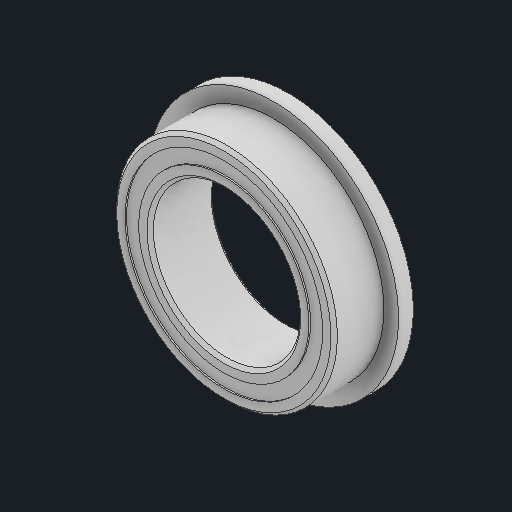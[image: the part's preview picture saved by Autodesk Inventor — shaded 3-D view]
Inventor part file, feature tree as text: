
AUTODESK INVENTOR PART (.ipt)
format: ipt  version: 2024 (Build 280153000, 153)  size: 592,896 bytes
history: native  units: in
note: dims shown in document units (in); Inventor stores cm internally (conversion verified against a paired STEP export)
features: other x11, revolve x5
ambient origin geometry x8: Origin, YZ Plane, XZ Plane, XY Plane, X Axis, Y Axis, Z Axis, Center Point
bodies: Solid1 (feature_tree), Solid2 (feature_tree), Solid3 (feature_tree), Solid4 (feature_tree), Solid5 (feature_tree), Solid6 (feature_tree), Solid7 (feature_tree), Solid8 (feature_tree), Solid9 (feature_tree), Solid10 (feature_tree), Solid11 (feature_tree), Solid12 (feature_tree), Solid13 (feature_tree), Solid14 (feature_tree), Solid15 (feature_tree), Solid16 (feature_tree)
feature tree (16):
  revolve  "Revolve3"  [1 undecoded]
  revolve  "Revolve4"  [1 undecoded]
  other  "CirPattern1[1]"
  other  "CirPattern1[2]"
  other  "CirPattern1[3]"
  other  "CirPattern1[4]"
  other  "CirPattern1[5]"
  other  "CirPattern1[6]"
  other  "CirPattern1[7]"
  other  "CirPattern1[8]"
  other  "CirPattern1[9]"
  other  "CirPattern1[10]"
  other  "CirPattern1[11]"
  revolve  "Revolve5[1]"  [1 undecoded]
  revolve  "Revolve5[2]"  [1 undecoded]
  revolve  "Revolve6"  [1 undecoded]
note: 5 required parameter values undecoded (feature->parameter linkage not recoverable at this tier; creation-order binding heuristic only, values carry confidence <= 0.55)
